# Revit family: EVID-C8.2HC
name_source: partatom
category: Communication Devices
revit_build: Autodesk Revit 2017 (Build: 20160225_1515(x64)
units: mm (PartAtom-declared; Revit-internal decimal feet)

## family parameters
Always vertical = Yes
Cut with Voids When Loaded = No
Maintain Annotation Orientation = Yes
OmniClass Number = 23.85.10.11.11.21
OmniClass Title = Speakers
Part Type = Normal
Room Calculation Point = No
Round Connector Dimension = Use Diameter
Shared = No
Work Plane-Based = Yes

## types (1)
- EVIDC8.2HC_Ceiling_Spkr_Sys-8_In_Thr_Pr
    ArchitectsAndEngineersSpecs = https://www.electrovoice.com
    BackLength = 284 mm  [stored 0.931759 ft]
    CTN = EVIDC8.2HC
    Default Elevation = 0 mm  [stored 0 ft]
    Depth = 340 mm  [stored 1.11549 ft]
    Description = 8" coaxial two-way with dual integrated Waveguides. Defined Coverage for High Ceiling Applications. Waveguide coupled Ti Tweeter. Full bandwith overload protection. Front baffle wattage tap adjustment. Integrated low loss matching transformer allows for either 70v/100v or 8-ohm operation. Includes tile bridge and mounting ring for easy installation. Integrated ported enclosure for extended bass reponse.
    Disclaimer = http://resource.boschsecurity.com
    FrontLength = 350 mm  [stored 1.14829 ft]
    Height = 340 mm  [stored 1.11549 ft]
    IfcExportAs = IfcBuildingElementProxy
    IfcExportType = IfcBuildingElementProxyType
    InstallationManual = https://www.electrovoice.com
    Manufacturer = Electro Voice
    ManufacturerURL = https://www.electrovoice.com
    MaterialRALColour = RAL9010
    ModelNumber = F.01U.117.588
    PlanningTools = http://www.electrovoice.com
    ProductInformation = https://www.electrovoice.com
    Uniclass2015Code = Pr_60_75_08_02
    Version = 1

note: [stored X ft] marks values corroborated as IEEE doubles in the binary element streams (Revit-internal decimal feet)

## geometry (parser evidence)
native form markers: Blend x2, Sweep x5
no freeform markers — native parametric forms only
